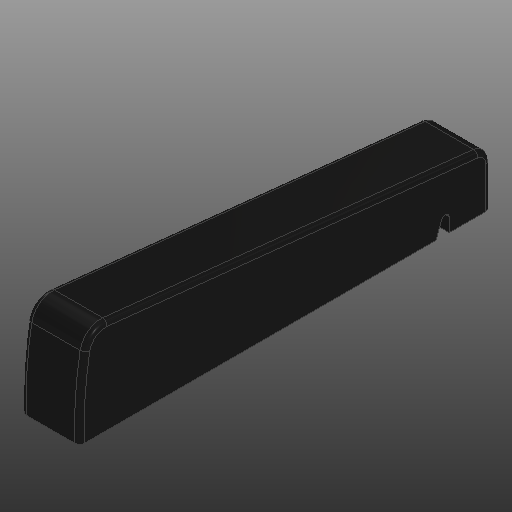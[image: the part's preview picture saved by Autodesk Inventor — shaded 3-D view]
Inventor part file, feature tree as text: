
AUTODESK INVENTOR PART (.ipt)
format: ipt  version: 2020 (Build 240168000, 168)  size: 268,288 bytes
history: native  units: in
note: dims shown in document units (in); Inventor stores cm internally (conversion verified against a paired STEP export)
features: other x3, extrude x3, fillet x2
ambient origin geometry x8: Origin, YZ Plane, XZ Plane, XY Plane, X Axis, Y Axis, Z Axis, Center Point
bodies: Solid1 (feature_tree)
feature tree (8):
  other  "Slot Start Plane"
  other  "Key Profile"
  extrude  "Key"  Depth=0.063in
  extrude  "Protrusion Cutout"  TaperAngle=0.0deg  [1 undecoded]
  fillet  "Front Fillet"  [1 undecoded]
  extrude  "Slot"  Depth=0.1181in
  fillet  "Edge Softening"  Radius=0.1374in
  other  "Slot Sketch"
note: 2 required parameter values undecoded (feature->parameter linkage not recoverable at this tier; creation-order binding heuristic only, values carry confidence <= 0.55)
